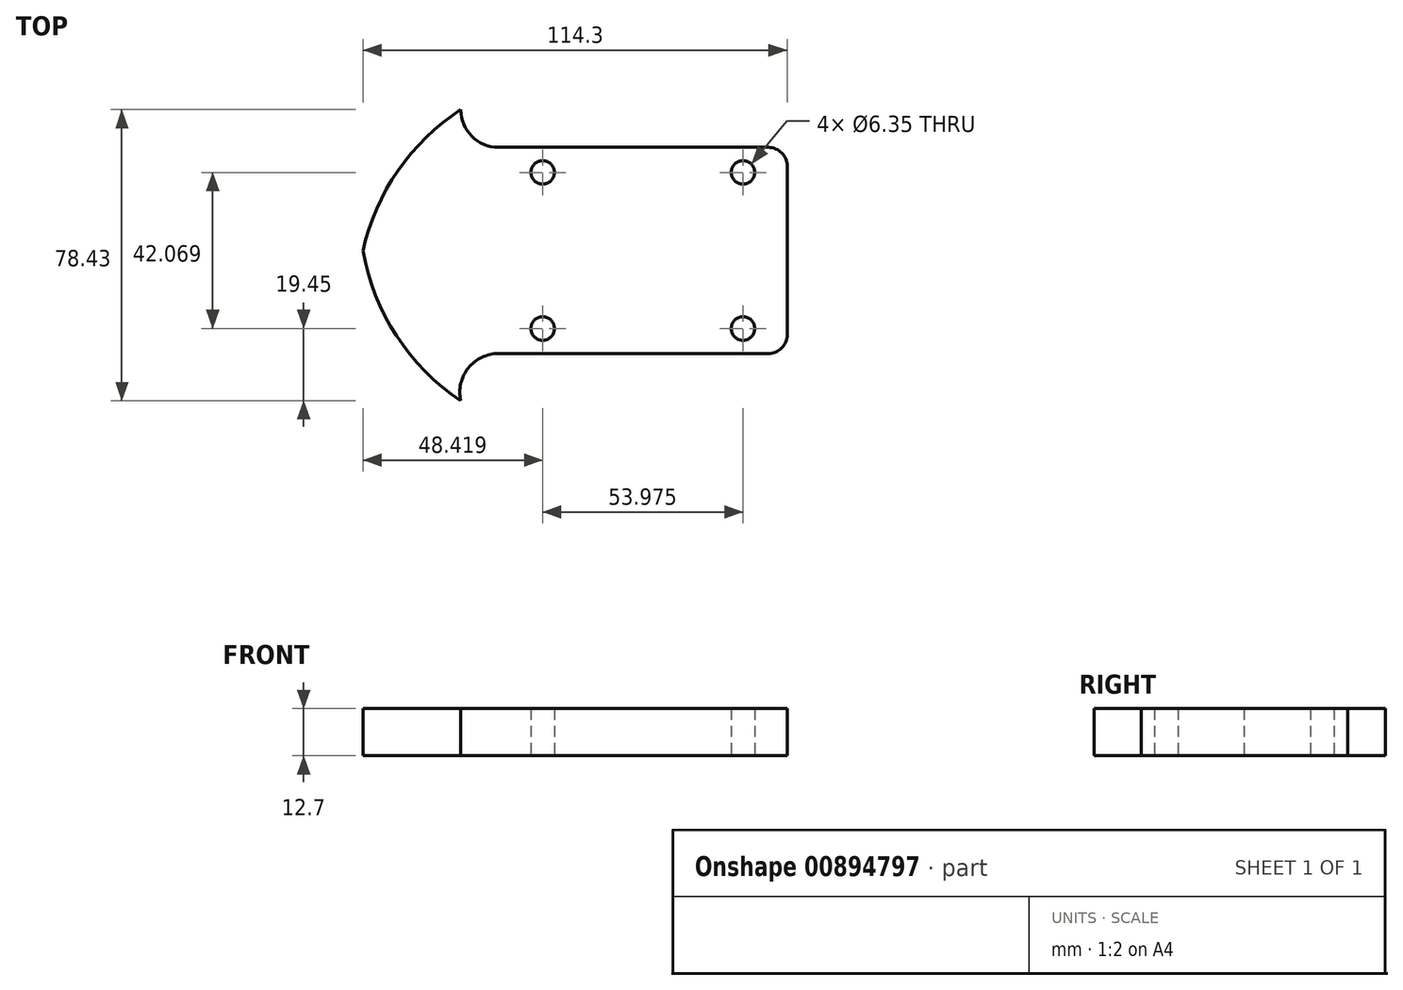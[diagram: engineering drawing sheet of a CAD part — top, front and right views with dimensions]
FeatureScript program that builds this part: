
annotation { "Feature Type Name" : "Feature", "Feature Type Description" : "" }
export const myFeature = defineFeature(function(context is Context, id is Id, definition is map)
    precondition{}
    {
        {
            var Q0;
            Q0=qCreatedBy(makeId("Top.planeOp"),FACE);
            var sketch = newSketch(context, id + "F0", { "sketchPlane" : qUnion([Q0])});
            skLineSegment(sketch, "E0.bottom", {"start": v(27.17, -20.9) * mm, "end": v(-26.8, -20.9) * mm, "construction": true});
            skLineSegment(sketch, "E0.top", {"start": v(27.17, 21.17) * mm, "end": v(-26.8, 21.17) * mm, "construction": true});
            skLineSegment(sketch, "E0.left", {"start": v(27.17, -20.9) * mm, "end": v(27.17, 21.17) * mm, "construction": true});
            skLineSegment(sketch, "E0.right", {"start": v(-26.8, -20.9) * mm, "end": v(-26.8, 21.17) * mm, "construction": true});
            skPoint(sketch, "E0.middle", {"position": v(0.19, 0.13) * mm});
            skCircle(sketch, "E1", {"center": v(-26.8, 21.17) * mm, "radius": 3.18 * mm});
            skCircle(sketch, "E2", {"center": v(27.17, 21.17) * mm, "radius": 3.18 * mm});
            skCircle(sketch, "E3", {"center": v(27.17, -20.9) * mm, "radius": 3.18 * mm});
            skCircle(sketch, "E4", {"center": v(-26.8, -20.9) * mm, "radius": 3.18 * mm});
            skLineSegment(sketch, "E5.bottom", {"start": v(39.08, -27.65) * mm, "end": v(-38.7, -27.65) * mm});
            skLineSegment(sketch, "E5.top", {"start": v(39.08, 27.92) * mm, "end": v(-38.7, 27.92) * mm});
            skLineSegment(sketch, "E5.left", {"start": v(39.08, -27.65) * mm, "end": v(39.08, 27.92) * mm});
            skLineSegment(sketch, "E5.right", {"start": v(-38.7, -27.65) * mm, "end": v(-38.7, 27.92) * mm, "construction": true});
            skLineSegment(sketch, "E6", {"start": v(-48.87, 38.08) * mm, "end": v(-48.87, -40.35) * mm, "construction": true});
            skArc(sketch, "E7", {"start": v(-38.7, -27.65) * mm, "mid": v(-46.84, -31.55) * mm, "end": v(-48.87, -40.35) * mm});
            skArc(sketch, "E8", {"start": v(-48.87, 38.08) * mm, "mid": v(-45.9, 30.9) * mm, "end": v(-38.7, 27.92) * mm});
            skArc(sketch, "E9", {"start": v(-48.87, 38.08) * mm, "mid": v(-65.79, 21.63) * mm, "end": v(-75.22, 0) * mm});
            skArc(sketch, "E10", {"start": v(-75.22, 0) * mm, "mid": v(-66.19, -22.88) * mm, "end": v(-48.87, -40.35) * mm});
            skSolve(sketch);
        }
        {
            var Q0;
            Q0 = qSketchRegion(id + "F0", true);
            extrude(context, id + "F1", {"entities" : qUnion([Q0]), "depth" : 12.7 * mm, "offsetDistance" : 25.4 * mm});
        }
        {
            var Q0;
            Q0=makeQuery(id+"F1.opExtrude","SWEPT_EDGE",EDGE,{"disambiguationData":[OSD([sQuery(id+"F0.wireOp",EDGE,"E5.bottom"),sQuery(id+"F0.wireOp",EDGE,"E5.left")])]});
            var Q1;
            Q1=makeQuery(id+"F1.opExtrude","SWEPT_EDGE",EDGE,{"disambiguationData":[OSD([sQuery(id+"F0.wireOp",EDGE,"E5.top"),sQuery(id+"F0.wireOp",EDGE,"E5.left")])]});
            fillet(context, id + "F2", {"entities" : qUnion([Q0, Q1]), "radius" : 5.08 * mm, "tangentPropagation" : true, "allowEdgeOverflow" : false});
        }
    });
